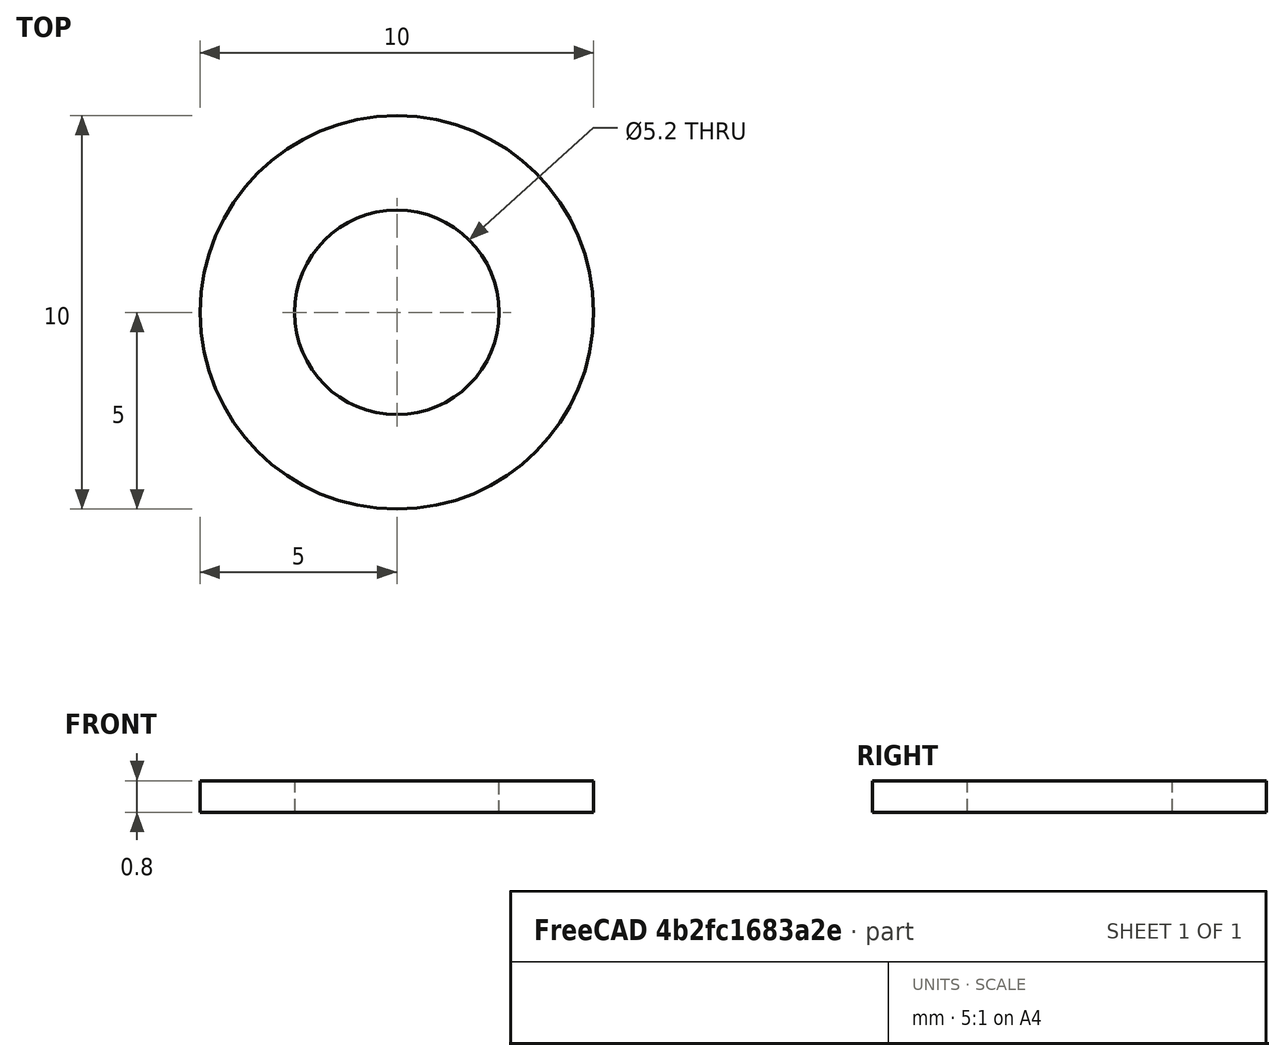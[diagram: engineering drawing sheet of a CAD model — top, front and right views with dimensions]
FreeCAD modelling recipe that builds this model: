
FCSTD DOCUMENT  (FreeCAD 0.20R29410 (Git))
Label: FM3_LuerSpacer
License: All rights reserved
LicenseURL: http://en.wikipedia.org/wiki/All_rights_reserved
objects: Sketcher::SketchObject×1, PartDesign::Pad×1, PartDesign::Body×1
note: 4 computed .brp shape members not serialized (recipe doc carries the construction recipe); baked Part::Feature solids carry a one-line shape summary decoded from their .brp

FEATURE [Sketcher::SketchObject] Sketch
  FullyConstrained = true
  MapMode = 5
  Support = -> [XY_Plane]
  sketch-geometry (2):
    g0: Circle CenterX=0 CenterY=0 CenterZ=0 NormalX=0 NormalY=0 NormalZ=1 AngleXU=0 Radius=2.6
    g1: Circle CenterX=0 CenterY=0 CenterZ=0 NormalX=0 NormalY=0 NormalZ=1 AngleXU=0 Radius=5
  constraints (4):
    c: Coincident(g0,g-1)
    c: Coincident(g1,g0)
    c: Diameter(g0) = 5.2
    c: Diameter(g1) = 10
FEATURE [PartDesign::Pad] Pad
  Direction = (0,0,1)
  Length = 0.8
  Length2 = 10
  Profile = -> Sketch
  ReferenceAxis = -> Sketch [N_Axis]
  Type = 0
FEATURE [PartDesign::Body] Body
  Group = -> [Sketch,Pad]
  Origin = -> Origin
  Tip = -> Pad
